# Revit family: RN 86002-xx Optiflex-Verteiler gekröpft
name_source: partatom
category: HLS-Bauteile
units: mm (PartAtom-declared; Revit-internal decimal feet)

## family parameters
Arbeitsebenenbasiert = Nein
Beim Laden mit Abzugskörper schneiden = Nein
Bemaßung runder Anschluss = Durchmesser verwenden
Gemeinsam genutzt = Nein
Immer vertikal = Ja
Klassifizierung = Keine
Raumberechnungspunkt = Nein
Teiletyp = Normal

## types (5) — shared parameters
DN1 = 20 mm  [stored 0.0656168 ft]
G1 = 20 mm  [stored 0.0656168 ft]
Hersteller = R. Nussbaum AG
L1 = 29 mm  [stored 0.0951444 ft]
L2 = 58 mm  [stored 0.190289 ft]
L3 = 30 mm  [stored 0.0984252 ft]
L5 = 32 mm  [stored 0.104987 ft]
RN_DNa = 25 mm  [stored 0.082021 ft]
RN_Dd1 = 75 mm
RN_Ddi = 35 mm  [stored 0.114829 ft]
RN_tab = RN_86002
Verbindung_1_Durchmesser = 25 mm  [stored 0.082021 ft]
Verbindung_2_Durchmesser = 20 mm  [stored 0.0656168 ft]
Verbindung_3_Durchmesser = 20 mm  [stored 0.0656168 ft]
Verbindung_4_Durchmesser = 25 mm  [stored 0.082021 ft]
p6 = Nein
p7 = Nein
p8 = Nein
z = 15 mm  [stored 0.0492126 ft]
z1 = 14 mm  [stored 0.0459318 ft]
zero-valued in all types: vpindex

## per-type parameters (varying)
| type | Beschreibung | L | N | RN_Beschreibung | Typenkommentare | URL | p1 | p2 | p3 | p4 | p5 | pindex |
| 86002.21 | DN20x1 | 58 mm  [stored 0.190289 ft] | 1 | DN20x1 | 86002.21 Optiflex-Verteiler gekröpft, 1 - fach mit Innengewinde |  | Ja | Nein | Nein | Nein | Nein | 1 |
| 86002.22 | DN20x2 | 116 mm | 2 | DN20x2 | 86002.22 Optiflex-Verteiler gekröpft, 2 - fach mit Innengewinde |  | Nein | Ja | Nein | Nein | Nein | 2 |
| 86002.23 | DN20x3 | 174 mm  [stored 0.570866 ft] | 3 | DN20x3 | 86002.23 Optiflex-Verteiler gekröpft, 3 - fach mit Innengewinde | https://www.nussbaum.ch | Nein | Nein | Ja | Nein | Nein | 3 |
| 86002.24 | DN20x4 | 232 mm | 4 | DN20x4 | 86002.24 Optiflex-Verteiler gekröpft, 4 - fach mit Innengewinde |  | Nein | Nein | Nein | Ja | Nein | 4 |
| 86002.25 | DN20x5 | 290 mm | 5 | DN20x5 | 86002.25 Optiflex-Verteiler gekröpft, 5 - fach mit Innengewinde | https://www.nussbaum.ch | Nein | Nein | Nein | Nein | Ja | 5 |

note: column(s) folded — value = type name in every type: RN_ArtNr

note: [stored X ft] marks values corroborated as IEEE doubles in the binary element streams (Revit-internal decimal feet)
